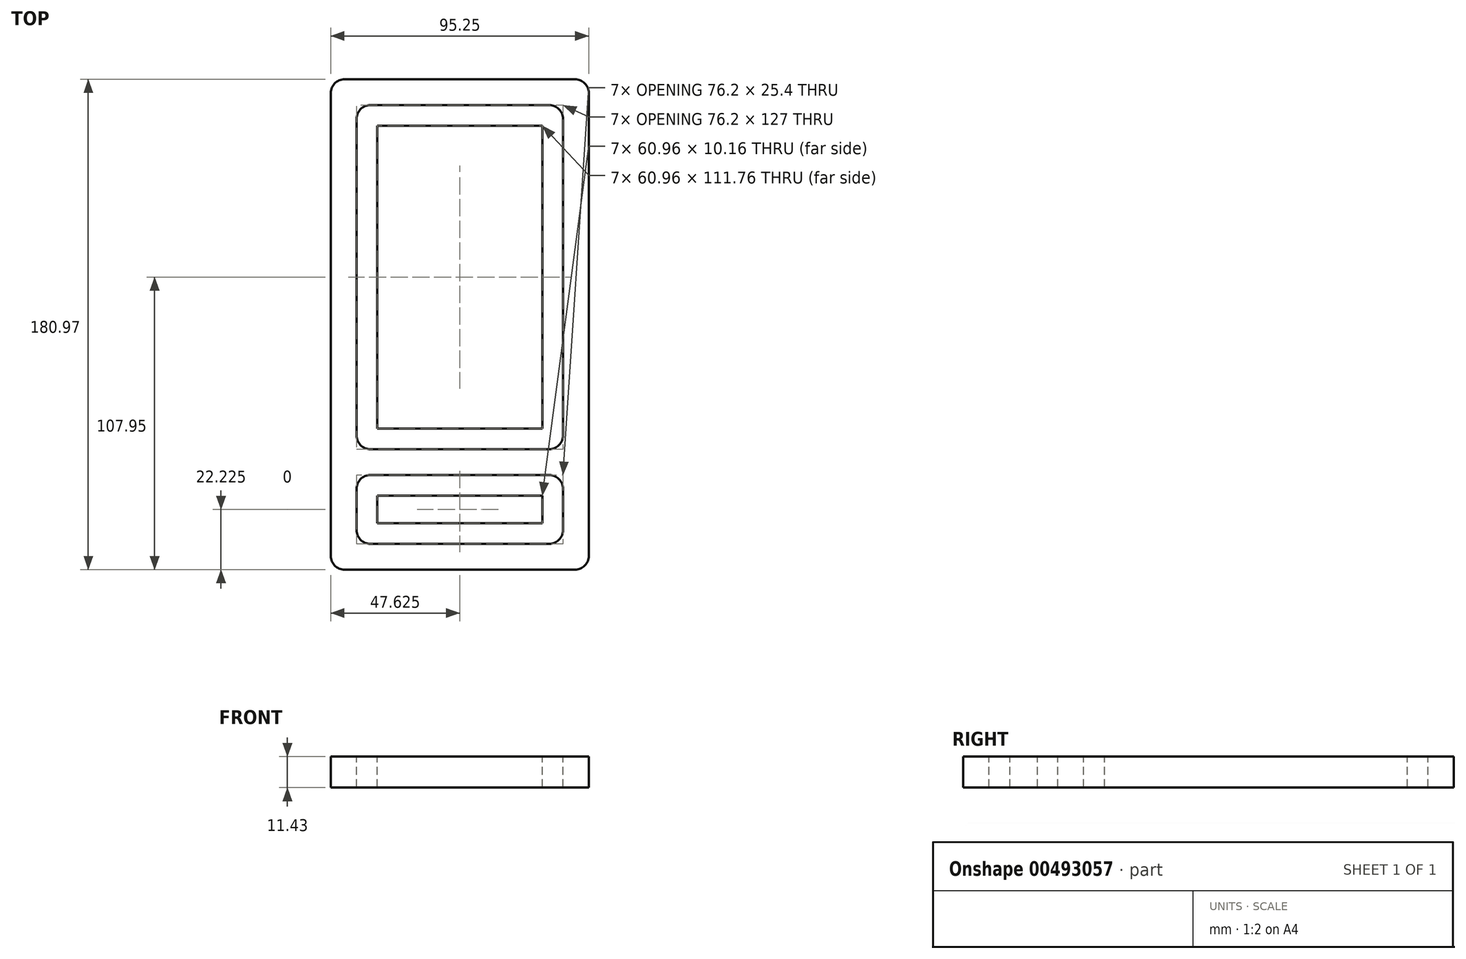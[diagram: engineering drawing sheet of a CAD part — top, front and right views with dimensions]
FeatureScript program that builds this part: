
annotation { "Feature Type Name" : "Feature", "Feature Type Description" : "" }
export const myFeature = defineFeature(function(context is Context, id is Id, definition is map)
    precondition{}
    {
        {
            var Q0;
            Q0=qCreatedBy(makeId("Top.planeOp"),FACE);
            var sketch = newSketch(context, id + "F0", { "sketchPlane" : qUnion([Q0])});
            skLineSegment(sketch, "E0.bottom", {"start": v(0, 180.98) * mm, "end": v(95.25, 180.98) * mm});
            skLineSegment(sketch, "E0.top", {"start": v(0, 0) * mm, "end": v(95.25, 0) * mm});
            skLineSegment(sketch, "E0.left", {"start": v(0, 180.98) * mm, "end": v(0, 0) * mm});
            skLineSegment(sketch, "E0.right", {"start": v(95.25, 180.98) * mm, "end": v(95.25, 0) * mm});
            skSolve(sketch);
        }
        {
            var Q0;
            Q0 = qSketchRegion(id + "F0", true);
            extrude(context, id + "F1", {"entities" : qUnion([Q0]), "depth" : 11.43 * mm});
        }
        {
            var Q0;
            Q0=makeQuery(id+"F1.opExtrude","CAP_FACE",FACE,{"disambiguationData":[OSD([sQuery(id+"F0.wireOp",EDGE,"E0.bottom"),sQuery(id+"F0.wireOp",EDGE,"E0.top"),sQuery(id+"F0.wireOp",EDGE,"E0.left"),sQuery(id+"F0.wireOp",EDGE,"E0.right")])],"isStart":false});
            var sketch = newSketch(context, id + "F2", { "sketchPlane" : qUnion([Q0])});
            skLineSegment(sketch, "E1.bottom", {"start": v(9.52, 171.45) * mm, "end": v(85.72, 171.45) * mm});
            skLineSegment(sketch, "E1.top", {"start": v(9.52, 44.45) * mm, "end": v(85.72, 44.45) * mm});
            skLineSegment(sketch, "E1.left", {"start": v(9.52, 171.45) * mm, "end": v(9.52, 44.45) * mm});
            skLineSegment(sketch, "E1.right", {"start": v(85.73, 171.45) * mm, "end": v(85.73, 44.45) * mm});
            skLineSegment(sketch, "E2.bottom", {"start": v(85.73, 9.53) * mm, "end": v(9.52, 9.52) * mm});
            skLineSegment(sketch, "E2.top", {"start": v(85.72, 34.93) * mm, "end": v(9.52, 34.92) * mm});
            skLineSegment(sketch, "E2.left", {"start": v(85.73, 9.53) * mm, "end": v(85.73, 34.93) * mm});
            skLineSegment(sketch, "E2.right", {"start": v(9.52, 9.52) * mm, "end": v(9.52, 34.92) * mm});
            skLineSegment(sketch, "E3.0", {"start": v(17.14, 163.83) * mm, "end": v(78.1, 163.83) * mm});
            skLineSegment(sketch, "E3.1", {"start": v(17.14, 163.83) * mm, "end": v(17.14, 52.07) * mm});
            skLineSegment(sketch, "E3.2", {"start": v(17.14, 52.07) * mm, "end": v(78.1, 52.07) * mm});
            skLineSegment(sketch, "E3.3", {"start": v(78.1, 163.83) * mm, "end": v(78.1, 52.07) * mm});
            skLineSegment(sketch, "E4.0", {"start": v(78.1, 27.3) * mm, "end": v(17.14, 27.3) * mm});
            skLineSegment(sketch, "E4.1", {"start": v(78.1, 17.15) * mm, "end": v(78.1, 27.3) * mm});
            skLineSegment(sketch, "E4.2", {"start": v(78.1, 17.15) * mm, "end": v(17.14, 17.14) * mm});
            skLineSegment(sketch, "E4.3", {"start": v(17.14, 17.14) * mm, "end": v(17.14, 27.3) * mm});
            skSolve(sketch);
        }
        {
            var Q0;
            Q0 = qSketchRegion(id + "F2", true);
            extrude(context, id + "F3", {"entities" : qUnion([Q0]), "operationType" : NewBodyOperationType.REMOVE, "oppositeDirection" : true, "depth" : 11.3 * mm});
        }
        {
            var Q0;
            Q0=makeQuery(id+"F1.opExtrude","SWEPT_EDGE",EDGE,{"disambiguationData":[OSD([sQuery(id+"F0.wireOp",EDGE,"E0.top"),sQuery(id+"F0.wireOp",EDGE,"E0.left")])]});
            var Q1;
            Q1=makeQuery(id+"F3.boolean.opBoolean","COPY",EDGE,{"derivedFrom":makeQuery(id+"F3.opExtrude","SWEPT_EDGE",EDGE,{"disambiguationData":[OSD([sQuery(id+"F2.wireOp",EDGE,"E2.top"),sQuery(id+"F2.wireOp",EDGE,"E2.right")])]})});
            var Q2;
            Q2=makeQuery(id+"F1.opExtrude","SWEPT_EDGE",EDGE,{"disambiguationData":[OSD([sQuery(id+"F0.wireOp",EDGE,"E0.top"),sQuery(id+"F0.wireOp",EDGE,"E0.right")])]});
            var Q3;
            Q3=makeQuery(id+"F3.boolean.opBoolean","COPY",EDGE,{"derivedFrom":makeQuery(id+"F3.opExtrude","SWEPT_EDGE",EDGE,{"disambiguationData":[OSD([sQuery(id+"F2.wireOp",EDGE,"E2.top"),sQuery(id+"F2.wireOp",EDGE,"E2.left")])]})});
            var Q4;
            Q4=makeQuery(id+"F3.boolean.opBoolean","COPY",EDGE,{"derivedFrom":makeQuery(id+"F3.opExtrude","SWEPT_EDGE",EDGE,{"disambiguationData":[OSD([sQuery(id+"F2.wireOp",EDGE,"E2.bottom"),sQuery(id+"F2.wireOp",EDGE,"E2.right")])]})});
            var Q5;
            Q5=makeQuery(id+"F3.boolean.opBoolean","COPY",EDGE,{"derivedFrom":makeQuery(id+"F3.opExtrude","SWEPT_EDGE",EDGE,{"disambiguationData":[OSD([sQuery(id+"F2.wireOp",EDGE,"E2.bottom"),sQuery(id+"F2.wireOp",EDGE,"E2.left")])]})});
            var Q6;
            Q6=makeQuery(id+"F3.boolean.opBoolean","COPY",EDGE,{"derivedFrom":makeQuery(id+"F3.opExtrude","SWEPT_EDGE",EDGE,{"disambiguationData":[OSD([sQuery(id+"F2.wireOp",EDGE,"E1.top"),sQuery(id+"F2.wireOp",EDGE,"E1.right")])]})});
            var Q7;
            Q7=makeQuery(id+"F3.boolean.opBoolean","COPY",EDGE,{"derivedFrom":makeQuery(id+"F3.opExtrude","SWEPT_EDGE",EDGE,{"disambiguationData":[OSD([sQuery(id+"F2.wireOp",EDGE,"E1.top"),sQuery(id+"F2.wireOp",EDGE,"E1.left")])]})});
            var Q8;
            Q8=makeQuery(id+"F1.opExtrude","SWEPT_EDGE",EDGE,{"disambiguationData":[OSD([sQuery(id+"F0.wireOp",EDGE,"E0.bottom"),sQuery(id+"F0.wireOp",EDGE,"E0.left")])]});
            var Q9;
            Q9=makeQuery(id+"F1.opExtrude","SWEPT_EDGE",EDGE,{"disambiguationData":[OSD([sQuery(id+"F0.wireOp",EDGE,"E0.bottom"),sQuery(id+"F0.wireOp",EDGE,"E0.right")])]});
            var Q10;
            Q10=makeQuery(id+"F3.boolean.opBoolean","COPY",EDGE,{"derivedFrom":makeQuery(id+"F3.opExtrude","SWEPT_EDGE",EDGE,{"disambiguationData":[OSD([sQuery(id+"F2.wireOp",EDGE,"E1.bottom"),sQuery(id+"F2.wireOp",EDGE,"E1.right")])]})});
            var Q11;
            Q11=makeQuery(id+"F3.boolean.opBoolean","COPY",EDGE,{"derivedFrom":makeQuery(id+"F3.opExtrude","SWEPT_EDGE",EDGE,{"disambiguationData":[OSD([sQuery(id+"F2.wireOp",EDGE,"E1.bottom"),sQuery(id+"F2.wireOp",EDGE,"E1.left")])]})});
            fillet(context, id + "F4", {"entities" : qUnion([Q0, Q1, Q2, Q3, Q4, Q5, Q6, Q7, Q8, Q9, Q10, Q11]), "radius" : 5.08 * mm, "tangentPropagation" : true, "allowEdgeOverflow" : false});
        }
    });
